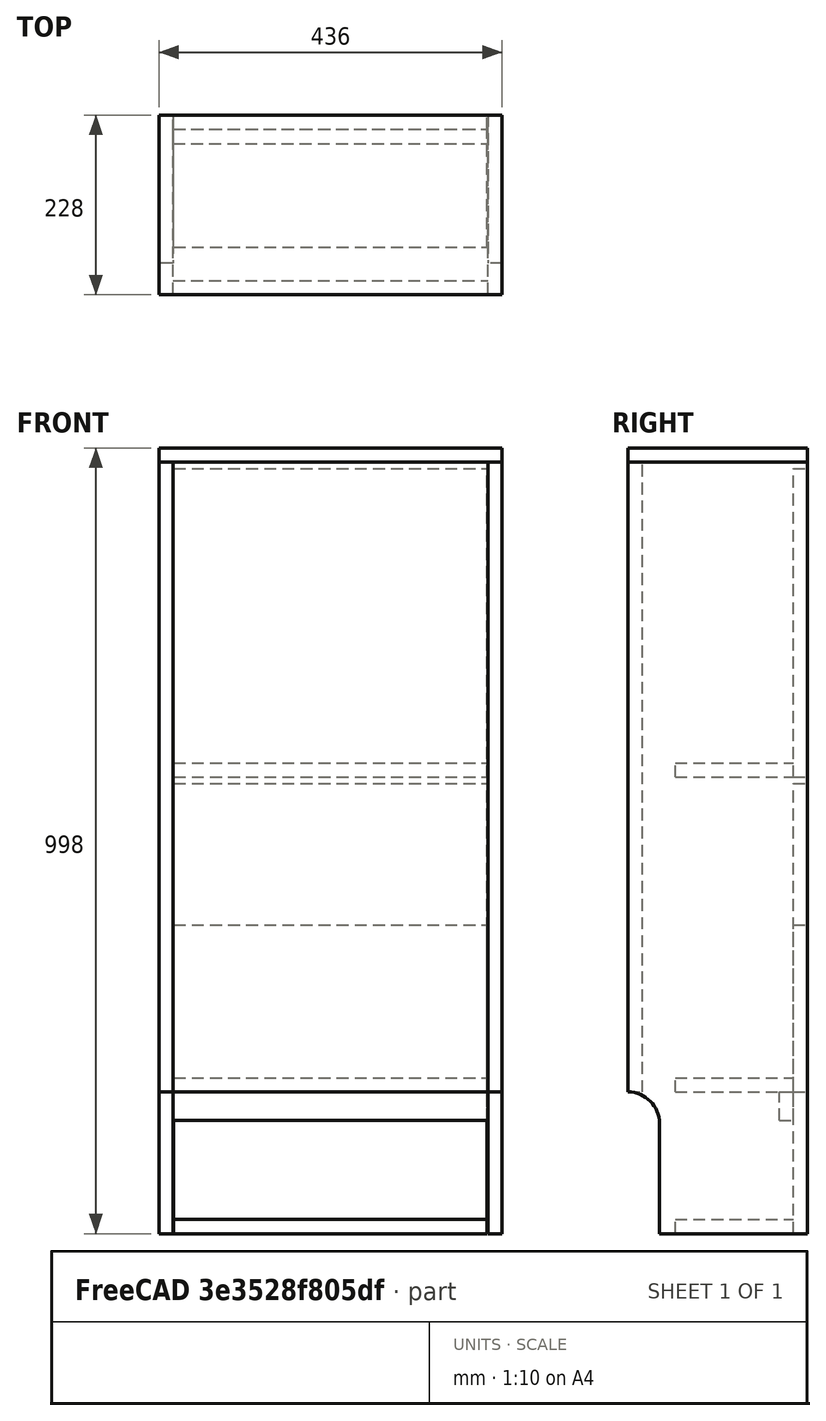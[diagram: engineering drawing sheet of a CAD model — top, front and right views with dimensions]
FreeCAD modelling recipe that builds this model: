
FCSTD DOCUMENT  (FreeCAD 0.20R)
Label: shoe_rack
License: All rights reserved
LicenseURL: http://en.wikipedia.org/wiki/All_rights_reserved
objects: TechDraw::DrawViewDimension×11, Part::FeaturePython×7, Part::Box×5, App::DocumentObjectGroup×4, App::Part×3, PartDesign::FeatureBase×2, TechDraw::DrawViewPart×2, Spreadsheet::Sheet×1, Sketcher::SketchObject×1, Part::Part2DObjectPython×1, PartDesign::Pad×1, PartDesign::Body×1, TechDraw::DrawSVGTemplate×1, TechDraw::DrawPage×1
note: 19 computed .brp shape members not serialized (recipe doc carries the construction recipe); baked Part::Feature solids carry a one-line shape summary decoded from their .brp

FEATURE [Spreadsheet::Sheet] Spreadsheet  label="main"
  cells = A1=Thickness; B1(Thickness)=18; A2=PanelHeight; B2(PanelHeight)=400; A3=NPanels; B3(NPanels)=2; A5=InnerWidth; B5(InnerWidth)=400; A6=InnerHeight; B6(InnerHeight)==PanelHeight * NPanels; A7=InnerDepth; B7(InnerDepth)==300 - 6 * Thickness; A9=DrawerHGap; B9(DrawerHGap)=1; A10=DrawerVGap; B10(DrawerVGap)=8; A12=DrawerWidth; B12(DrawerWidth)==InnerWidth - 2 * DrawerHGap; A13=DrawerHeight; B13(DrawerHeight)==PanelHeight - DrawerVGap; A14=DrawerDepth; B14(DrawerDepth)=150; A16=RebarHeight; B16(RebarHeight)==2 * Thickness; A18=FootHeight; B18(FootHeight)=180; A19=FootGap; B19(FootGap)=40; A20=SideHeight; B20(SideHeight)==InnerHeight + FootHeight; A22=TotalWidth; B22(TotalWidth)==2 * Thickness + InnerWidth; A23=TotalHeight; B23(TotalHeight)==SideHeight + Thickness; A24=TotalDepth; B24(TotalDepth)==2 * Thickness + InnerDepth
FEATURE [Sketcher::SketchObject] Sketch  label="Main_LeftSide"
  FullyConstrained = true
  Placement = pos=(0,0,0) rot=(0.57735,-0.57735,-0.57735;2.0944rad)
  expr: Constraints[13] = <<main>>.TotalDepth
  expr: Constraints[14] = <<main>>.SideHeight
  expr: Constraints[15] = <<main>>.FootHeight
  expr: Constraints[16] = <<main>>.FootGap
  sketch-geometry (6):
    g0: LineSegment StartX=-40 StartY=0 StartZ=0 EndX=-40 EndY=140 EndZ=0
    g1: LineSegment StartX=2.4e-15 StartY=180 StartZ=0 EndX=0 EndY=980 EndZ=0
    g2: LineSegment StartX=0 StartY=980 StartZ=0 EndX=-228 EndY=980 EndZ=0
    g3: LineSegment StartX=-228 StartY=980 StartZ=0 EndX=-228 EndY=0 EndZ=0
    g4: LineSegment StartX=-228 StartY=0 StartZ=0 EndX=-40 EndY=0 EndZ=0
    g5: ArcOfCircle CenterX=0 CenterY=140 CenterZ=0 NormalX=0 NormalY=0 NormalZ=1 AngleXU=0 Radius=40 StartAngle=1.5708 EndAngle=3.14159
  constraints (18):
    c: PointOnObject(g0,g-1)
    c: PointOnObject(g1,g-2)
    c: PointOnObject(g1,g-2)
    c: Coincident(g1,g2)
    c: Coincident(g2,g3)
    c: PointOnObject(g3,g-1)
    c: Vertical(g3)
    c: Coincident(g3,g4)
    c: Coincident(g4,g0)
    c: Horizontal(g2)
    c: Vertical(g0)
    c: Coincident(g5,g1)
    c: Tangent(g5,g0) = 1.5708
    c: DistanceX(g2,g2) = 228
    c: DistanceY(g3,g3) = 980
    c: DistanceY(g-1,g1) = 180
    c: DistanceX(g0,g-1) = 40
    c: PointOnObject(g5,g-2)
FEATURE [App::DocumentObjectGroup] Group  label="Main_Sketches"
  Group = -> [Sketch]
FEATURE [Part::Part2DObjectPython] Clone2D  label="Main_LeftSide (2D)"  # Draft 2D object (typed FeaturePython)
  Fuse = false
  Objects = -> [Sketch]
  Placement = pos=(0,0,0) rot=(0.57735,-0.57735,-0.57735;2.0944rad)
  Scale = (1,1,1)
FEATURE [PartDesign::FeatureBase] BaseFeature
  BaseFeature = -> Clone2D
FEATURE [PartDesign::Pad] Pad  label="Main_PadLeftSide"
  BaseFeature = -> BaseFeature
  Direction = (-1,0,0)
  Length = 18
  Length2 = 10
  Profile = -> Clone2D
  ReferenceAxis = -> Clone2D [N_Axis]
  Type = 0
  expr: Length = <<main>>.Thickness
FEATURE [Part::Box] Box  label="Part_Top"
  AttacherType = Attacher::AttachEngine3D
  Height = 18
  Length = 436
  Placement = pos=(-218,0,980) rot=(0,0,1;0rad)
  Width = 228
  expr: .Placement.Base.x = -Length / 2
  expr: .Placement.Base.z = <<main>>.SideHeight
  expr: Height = <<main>>.Thickness
  expr: Length = <<main>>.TotalWidth
  expr: Width = <<main>>.TotalDepth
FEATURE [Part::Box] Box001  label="Main_DrawerBottom"
  AttacherType = Attacher::AttachEngine3D
  Height = 18
  Length = 398
  Placement = pos=(-199,60,0) rot=(0,0,1;0rad)
  Width = 150
  expr: .Placement.Base.x = -Length / 2
  expr: .Placement.Base.y = <<Main_DrawerFront>>.Placement.Base.y - Width
  expr: Height = <<main>>.Thickness
  expr: Length = <<main>>.DrawerWidth
  expr: Width = <<main>>.DrawerDepth
FEATURE [Part::Box] Box002  label="Part_Back"
  AttacherType = Attacher::AttachEngine3D
  Height = 800
  Length = 400
  Placement = pos=(-200,0,180) rot=(0,0,1;0rad)
  Width = 18
  expr: .Placement.Base.x = -Length / 2
  expr: .Placement.Base.z = <<main>>.FootHeight
  expr: Height = <<main>>.InnerHeight
  expr: Length = <<main>>.InnerWidth
  expr: Width = <<main>>.Thickness
FEATURE [Part::Box] Box003  label="Main_Rebar"
  AttacherType = Attacher::AttachEngine3D
  Height = 36
  Length = 400
  Placement = pos=(-200,192,0) rot=(0,0,1;0rad)
  Width = 18
  expr: .Placement.Base.x = -Length / 2
  expr: .Placement.Base.y = <<main>>.InnerDepth
  expr: Height = <<main>>.RebarHeight
  expr: Length = <<main>>.InnerWidth
  expr: Width = <<main>>.Thickness
FEATURE [App::Part] Part  label="Part_Main_Rebar"
  Group = -> [Box003]
  Origin = -> Origin001
FEATURE [Part::FeaturePython] Clone002  label="Part_RebarTop"  # Draft clone (typed FeaturePython)
  AttacherType = Attacher::AttachEngine3D
  Fuse = false
  Objects = -> [Box003]
  Placement = pos=(-200,192,944) rot=(0,0,1;0rad)
  Scale = (1,1,1)
  expr: .Placement.Base.x = <<Main_Rebar>>.Placement.Base.x
  expr: .Placement.Base.y = <<Main_Rebar>>.Placement.Base.y
  expr: .Placement.Base.z = <<main>>.SideHeight - <<main>>.RebarHeight
FEATURE [Part::FeaturePython] Clone003  label="Part_RebarMiddle"  # Draft clone (typed FeaturePython)
  AttacherType = Attacher::AttachEngine3D
  Fuse = false
  Objects = -> [Clone002]
  Placement = pos=(-200,192,544) rot=(0,0,1;0rad)
  Scale = (1,1,1)
  expr: .Placement.Base.x = <<Main_Rebar>>.Placement.Base.x
  expr: .Placement.Base.y = <<Main_Rebar>>.Placement.Base.y
  expr: .Placement.Base.z = <<Part_RebarTop>>.Placement.Base.z - 1mm * <<main>>.PanelHeight
FEATURE [Part::FeaturePython] Clone004  label="Part_RebarBottom"  # Draft clone (typed FeaturePython)
  AttacherType = Attacher::AttachEngine3D
  Fuse = false
  Objects = -> [Clone003]
  Placement = pos=(-200,192,144) rot=(0,0,1;0rad)
  Scale = (1,1,1)
  expr: .Placement.Base.x = <<Main_Rebar>>.Placement.Base.x
  expr: .Placement.Base.y = <<Main_Rebar>>.Placement.Base.y
  expr: .Placement.Base.z = <<Part_RebarMiddle>>.Placement.Base.z - 1mm * <<main>>.PanelHeight
FEATURE [PartDesign::FeatureBase] BaseFeature001  label="Main_PadLeftSide001"
  BaseFeature = -> Pad
FEATURE [PartDesign::Body] Body  label="Body_PadLeftSide"
  BaseFeature = -> Pad
  Group = -> [BaseFeature001]
  Origin = -> Origin
  Tip = -> BaseFeature001
FEATURE [Part::FeaturePython] Clone  label="Part_LeftSide"  # Draft clone (typed FeaturePython)
  AttacherType = Attacher::AttachEngine3D
  Fuse = false
  Objects = -> [Body]
  Placement = pos=(-200,0,0) rot=(0,0,1;0rad)
  Scale = (1,1,1)
  expr: .Placement.Base.x = -<<main>>.TotalWidth / 2 + <<main>>.Thickness
FEATURE [Part::FeaturePython] Clone001  label="Part_RightSide"  # Draft clone (typed FeaturePython)
  AttacherType = Attacher::AttachEngine3D
  Fuse = false
  Objects = -> [Body]
  Placement = pos=(218,0,0) rot=(0,0,1;0rad)
  Scale = (1,1,1)
  expr: .Placement.Base.x = <<main>>.TotalWidth / 2
FEATURE [App::Part] Part002  label="Part_Main_Side"
  Group = -> [Body,Pad,Clone2D,BaseFeature]
  Origin = -> Origin003
FEATURE [Part::Box] Box004  label="Main_DrawerFront"
  AttacherType = Attacher::AttachEngine3D
  Height = 392
  Length = 398
  Placement = pos=(-199,210,0) rot=(0,0,1;0rad)
  Width = 18
  expr: .Placement.Base.x = -Length / 2
  expr: .Placement.Base.y = <<main>>.InnerDepth + <<main>>.Thickness
  expr: Height = <<main>>.DrawerHeight
  expr: Length = <<main>>.DrawerWidth
  expr: Width = <<main>>.Thickness
FEATURE [App::Part] Part001  label="Part_Main_Drawer"
  Group = -> [Box001,Box004]
  Origin = -> Origin002
FEATURE [App::DocumentObjectGroup] Group001  label="Main_Group"
  Group = -> [Part,Part001,Part002]
FEATURE [Part::FeaturePython] Clone005  label="Part_DrawerTop"  # Draft clone (typed FeaturePython)
  AttacherType = Attacher::AttachEngine3D
  Fuse = false
  Objects = -> [Part001]
  Placement = pos=(0,0,580) rot=(0,0,1;0rad)
  Scale = (1,1,1)
  expr: .Placement.Base.z = <<Part_Top>>.Placement.Base.z - <<main>>.PanelHeight * 1mm
FEATURE [Part::FeaturePython] Clone006  label="Part_DrawerMiddle"  # Draft clone (typed FeaturePython)
  AttacherType = Attacher::AttachEngine3D
  Fuse = false
  Objects = -> [Part001]
  Placement = pos=(0,0,180) rot=(0,0,1;0rad)
  Scale = (1,1,1)
  expr: .Placement.Base.z = <<Part_Top>>.Placement.Base.z - <<main>>.PanelHeight * 2 * 1mm
FEATURE [App::DocumentObjectGroup] Group002  label="Parts"
  Group = -> [Box,Clone,Clone001,Box002,Clone002,Clone003,Clone004,Clone005,Clone006]
FEATURE [TechDraw::DrawSVGTemplate] Template
  EditableTexts = Designed_by_Name=Designed by Name; Drawing_number=Drawing number; FC-Date=Date; FC-SC=Scale; FC-SH=Sheet; FC-Title=Title; Subtitle=Subtitle; Weight=Weight
  Height = 210
  Orientation = 1
  Width = 297
FEATURE [TechDraw::DrawViewPart] View
  CoarseView = false
  Direction = (-1,0,0)
  Focus = 100
  HardHidden = false
  IsoCount = 0
  IsoHidden = false
  IsoVisible = false
  LockPosition = false
  Perspective = false
  Rotation = 0
  Scale = 0.1
  ScaleType = 2
  SeamHidden = false
  SeamVisible = true
  SmoothHidden = false
  SmoothVisible = true
  Source = -> [Group002]
  X = 92.563
  XDirection = (0,-1,0)
  Y = 131.456
FEATURE [TechDraw::DrawViewPart] View001
  CoarseView = false
  Direction = (0,1,0)
  Focus = 100
  HardHidden = false
  IsoCount = 0
  IsoHidden = false
  IsoVisible = false
  LockPosition = false
  Perspective = false
  Rotation = 0
  Scale = 0.1
  ScaleType = 2
  SeamHidden = false
  SeamVisible = true
  SmoothHidden = false
  SmoothVisible = true
  Source = -> [Group002]
  X = 200.883
  XDirection = (-1,0,0)
  Y = 131.192
FEATURE [TechDraw::DrawViewDimension] Dimension
  AngleOverride = false
  Arbitrary = false
  ArbitraryTolerances = false
  EqualTolerance = true
  ExtensionAngle = 0
  FormatSpec = %.2w
  FormatSpecOverTolerance = %+.2w
  FormatSpecUnderTolerance = %+.2w
  Inverted = false
  LineAngle = 0
  LockPosition = false
  MeasureType = 1
  OverTolerance = 0
  References2D = -> [View]
  Rotation = 0
  ScaleType = 0
  TheoreticalExact = false
  Type = 1
  UnderTolerance = 0
  X = -0.215459
  Y = 63.1528
FEATURE [TechDraw::DrawViewDimension] Dimension001
  AngleOverride = false
  Arbitrary = false
  ArbitraryTolerances = false
  EqualTolerance = true
  ExtensionAngle = 0
  FormatSpec = %.2w
  FormatSpecOverTolerance = %+.2w
  FormatSpecUnderTolerance = %+.2w
  Inverted = false
  LineAngle = 0
  LockPosition = false
  MeasureType = 1
  OverTolerance = 0
  References2D = -> [View]
  Rotation = 0
  ScaleType = 0
  TheoreticalExact = false
  Type = 2
  UnderTolerance = 0
  X = 21.5316
  Y = 12.0202
FEATURE [TechDraw::DrawViewDimension] Dimension002
  AngleOverride = false
  Arbitrary = false
  ArbitraryTolerances = false
  EqualTolerance = true
  ExtensionAngle = 0
  FormatSpec = %.2w
  FormatSpecOverTolerance = %+.2w
  FormatSpecUnderTolerance = %+.2w
  Inverted = false
  LineAngle = 0
  LockPosition = false
  MeasureType = 1
  OverTolerance = 0
  References2D = -> [View]
  Rotation = 0
  ScaleType = 0
  TheoreticalExact = false
  Type = 2
  UnderTolerance = 0
  X = -26.2231
  Y = 34.0019
FEATURE [TechDraw::DrawViewDimension] Dimension003
  AngleOverride = false
  Arbitrary = false
  ArbitraryTolerances = false
  EqualTolerance = true
  ExtensionAngle = 0
  FormatSpec = %.2w
  FormatSpecOverTolerance = %+.2w
  FormatSpecUnderTolerance = %+.2w
  Inverted = false
  LineAngle = 0
  LockPosition = false
  MeasureType = 1
  OverTolerance = 0
  References2D = -> [View]
  Rotation = 0
  ScaleType = 0
  TheoreticalExact = false
  Type = 2
  UnderTolerance = 0
  X = -26.6289
  Y = -7.82404
FEATURE [TechDraw::DrawViewDimension] Dimension004
  AngleOverride = false
  Arbitrary = false
  ArbitraryTolerances = false
  EqualTolerance = true
  ExtensionAngle = 0
  FormatSpec = %.2w
  FormatSpecOverTolerance = %+.2w
  FormatSpecUnderTolerance = %+.2w
  Inverted = false
  LineAngle = 0
  LockPosition = false
  MeasureType = 1
  OverTolerance = 0
  References2D = -> [View]
  Rotation = 0
  ScaleType = 0
  TheoreticalExact = false
  Type = 2
  UnderTolerance = 0
  X = -27.2375
  Y = -37.9942
FEATURE [TechDraw::DrawViewDimension] Dimension005
  AngleOverride = false
  Arbitrary = false
  ArbitraryTolerances = false
  EqualTolerance = true
  ExtensionAngle = 0
  FormatSpec = %.2w
  FormatSpecOverTolerance = %+.2w
  FormatSpecUnderTolerance = %+.2w
  Inverted = false
  LineAngle = 0
  LockPosition = false
  MeasureType = 1
  OverTolerance = 0
  References2D = -> [View]
  Rotation = 0
  ScaleType = 0
  TheoreticalExact = false
  Type = 2
  UnderTolerance = 0
  X = 35.2507
  Y = 5.86056
FEATURE [TechDraw::DrawViewDimension] Dimension006
  AngleOverride = false
  Arbitrary = false
  ArbitraryTolerances = false
  EqualTolerance = true
  ExtensionAngle = 0
  FormatSpec = %.2w
  FormatSpecOverTolerance = %+.2w
  FormatSpecUnderTolerance = %+.2w
  Inverted = false
  LineAngle = 0
  LockPosition = false
  MeasureType = 1
  OverTolerance = 0
  References2D = -> [View001]
  Rotation = 0
  ScaleType = 0
  TheoreticalExact = false
  Type = 1
  UnderTolerance = 0
  X = 0.012576
  Y = 62.3413
FEATURE [TechDraw::DrawViewDimension] Dimension007
  AngleOverride = false
  Arbitrary = false
  ArbitraryTolerances = false
  EqualTolerance = true
  ExtensionAngle = 0
  FormatSpec = %.2w
  FormatSpecOverTolerance = %+.2w
  FormatSpecUnderTolerance = %+.2w
  Inverted = false
  LineAngle = 0
  LockPosition = false
  MeasureType = 1
  OverTolerance = 0
  References2D = -> [View]
  Rotation = 0
  ScaleType = 0
  TheoreticalExact = false
  Type = 2
  UnderTolerance = 0
  X = 21.9951
  Y = -40.4
FEATURE [TechDraw::DrawViewDimension] Dimension008
  AngleOverride = false
  Arbitrary = false
  ArbitraryTolerances = false
  EqualTolerance = true
  ExtensionAngle = 0
  FormatSpec = %.2w
  FormatSpecOverTolerance = %+.2w
  FormatSpecUnderTolerance = %+.2w
  Inverted = false
  LineAngle = 0
  LockPosition = false
  MeasureType = 1
  OverTolerance = 0
  References2D = -> [View]
  Rotation = 0
  ScaleType = 0
  TheoreticalExact = false
  Type = 1
  UnderTolerance = 0
  X = 17.9085
  Y = -57.7749
FEATURE [TechDraw::DrawViewDimension] Dimension009
  AngleOverride = false
  Arbitrary = false
  ArbitraryTolerances = false
  EqualTolerance = true
  ExtensionAngle = 0
  FormatSpec = %.2w
  FormatSpecOverTolerance = %+.2w
  FormatSpecUnderTolerance = %+.2w
  Inverted = false
  LineAngle = 0
  LockPosition = false
  MeasureType = 1
  OverTolerance = 0
  References2D = -> [View001]
  Rotation = 0
  ScaleType = 0
  TheoreticalExact = false
  Type = 1
  UnderTolerance = 0
  X = 0.012576
  Y = 26.6278
FEATURE [TechDraw::DrawViewDimension] Dimension010
  AngleOverride = false
  Arbitrary = false
  ArbitraryTolerances = false
  EqualTolerance = true
  ExtensionAngle = 0
  FormatSpec = %.2w
  FormatSpecOverTolerance = %+.2w
  FormatSpecUnderTolerance = %+.2w
  Inverted = false
  LineAngle = 0
  LockPosition = false
  MeasureType = 1
  OverTolerance = 0
  References2D = -> [View001]
  Rotation = 0
  ScaleType = 0
  TheoreticalExact = false
  Type = 1
  UnderTolerance = 0
  X = -0.190308
  Y = -38.275
FEATURE [TechDraw::DrawPage] Page001
  KeepUpdated = true
  NextBalloonIndex = 1
  ProjectionType = 0
  Template = -> Template
  Views = -> [View,View001,Dimension,Dimension001,Dimension002,Dimension003,Dimension004,Dimension005,Dimension006,Dimension007,Dimension008,Dimension009,Dimension010]
FEATURE [App::DocumentObjectGroup] Group003  label="Group"
  Group = -> [Page001]
